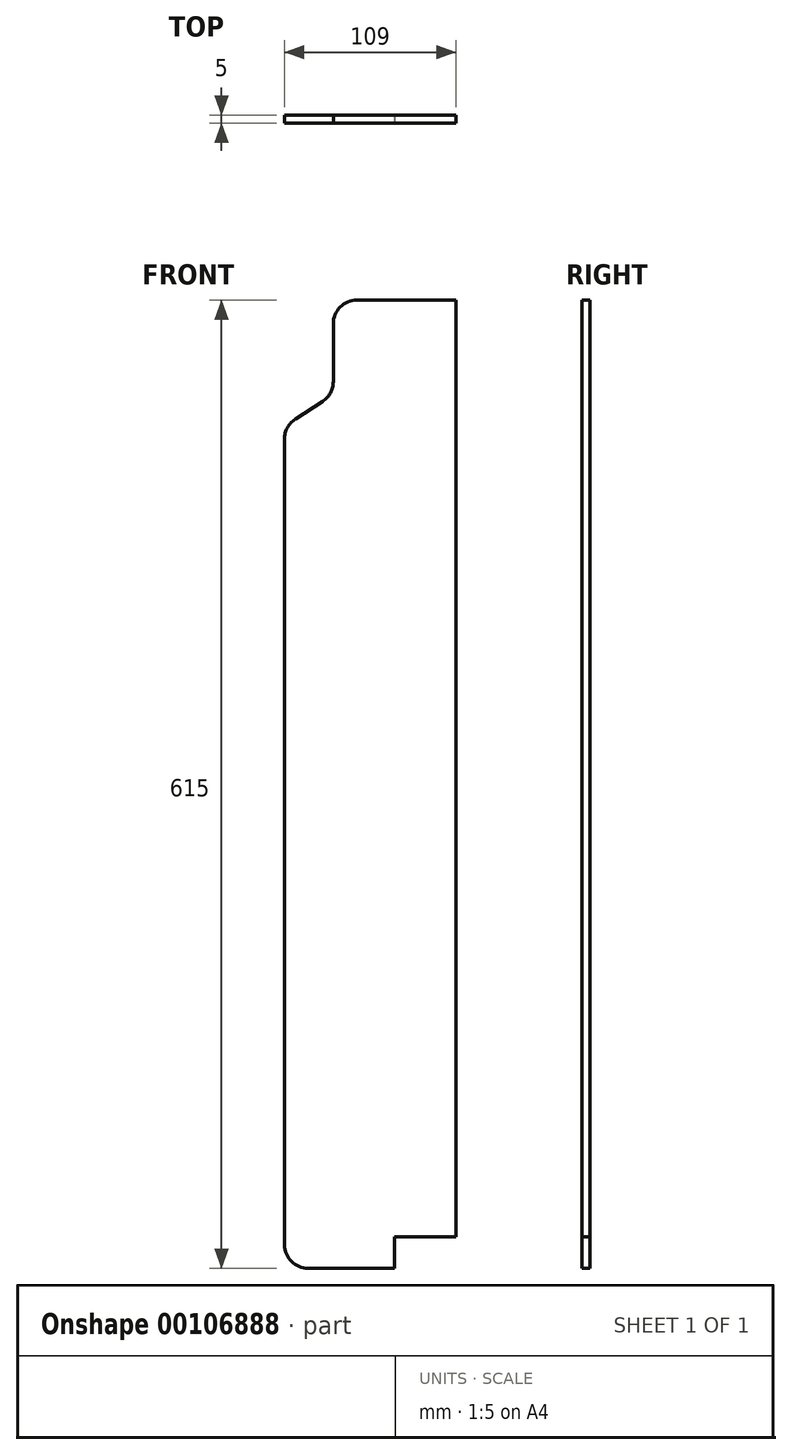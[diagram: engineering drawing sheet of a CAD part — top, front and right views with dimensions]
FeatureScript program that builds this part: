
annotation { "Feature Type Name" : "Feature", "Feature Type Description" : "" }
export const myFeature = defineFeature(function(context is Context, id is Id, definition is map)
    precondition{}
    {
        {
            var Q0;
            Q0=qCreatedBy(makeId("Front.planeOp"),FACE);
            var sketch = newSketch(context, id + "F0", { "sketchPlane" : qUnion([Q0])});
            skLineSegment(sketch, "E0", {"start": v(0, 0) * mm, "end": v(0, 595) * mm});
            skLineSegment(sketch, "E1", {"start": v(0, 595) * mm, "end": v(-63, 595) * mm});
            skLineSegment(sketch, "E2", {"start": v(-78, 580) * mm, "end": v(-78, 543.17) * mm});
            skLineSegment(sketch, "E3", {"start": v(-84.87, 530.57) * mm, "end": v(-102.13, 519.43) * mm});
            skLineSegment(sketch, "E4", {"start": v(-109, 506.83) * mm, "end": v(-109, -5) * mm});
            skLineSegment(sketch, "E5", {"start": v(-94, -20) * mm, "end": v(-39, -20) * mm});
            skLineSegment(sketch, "E6", {"start": v(-39, -20) * mm, "end": v(-39, 0) * mm});
            skLineSegment(sketch, "E7", {"start": v(-39, 0) * mm, "end": v(0, 0) * mm});
            skPoint(sketch, "E8.visualSharp", {"position": v(-78, 595) * mm});
            skArc(sketch, "E8.filletArc", {"start": v(-63, 595) * mm, "mid": v(-73.6, 590.6) * mm, "end": v(-78, 580) * mm});
            skPoint(sketch, "E9.visualSharp", {"position": v(-78, 535) * mm});
            skArc(sketch, "E9.filletArc", {"start": v(-84.87, 530.57) * mm, "mid": v(-79.83, 536) * mm, "end": v(-78, 543.17) * mm});
            skPoint(sketch, "E10.visualSharp", {"position": v(-109, 515) * mm});
            skArc(sketch, "E10.filletArc", {"start": v(-102.13, 519.43) * mm, "mid": v(-107.17, 514) * mm, "end": v(-109, 506.83) * mm});
            skPoint(sketch, "E11.visualSharp", {"position": v(-109, -20) * mm});
            skArc(sketch, "E11.filletArc", {"start": v(-109, -5) * mm, "mid": v(-104.6, -15.6) * mm, "end": v(-94, -20) * mm});
            skSolve(sketch);
        }
        {
            var Q0;
            Q0=makeQuery(id+"F0.imprint","IMPRINT",FACE,{"disambiguationData":[TD([[makeQuery(id+"F0.imprint","IMPRINT",EDGE,{"derivedFrom":sQuery(id+"F0.wireOp",EDGE,"E0")}),1.0]])]});
            extrude(context, id + "F1", {"entities" : qUnion([Q0]), "oppositeDirection" : true, "depth" : 5 * mm});
        }
    });
